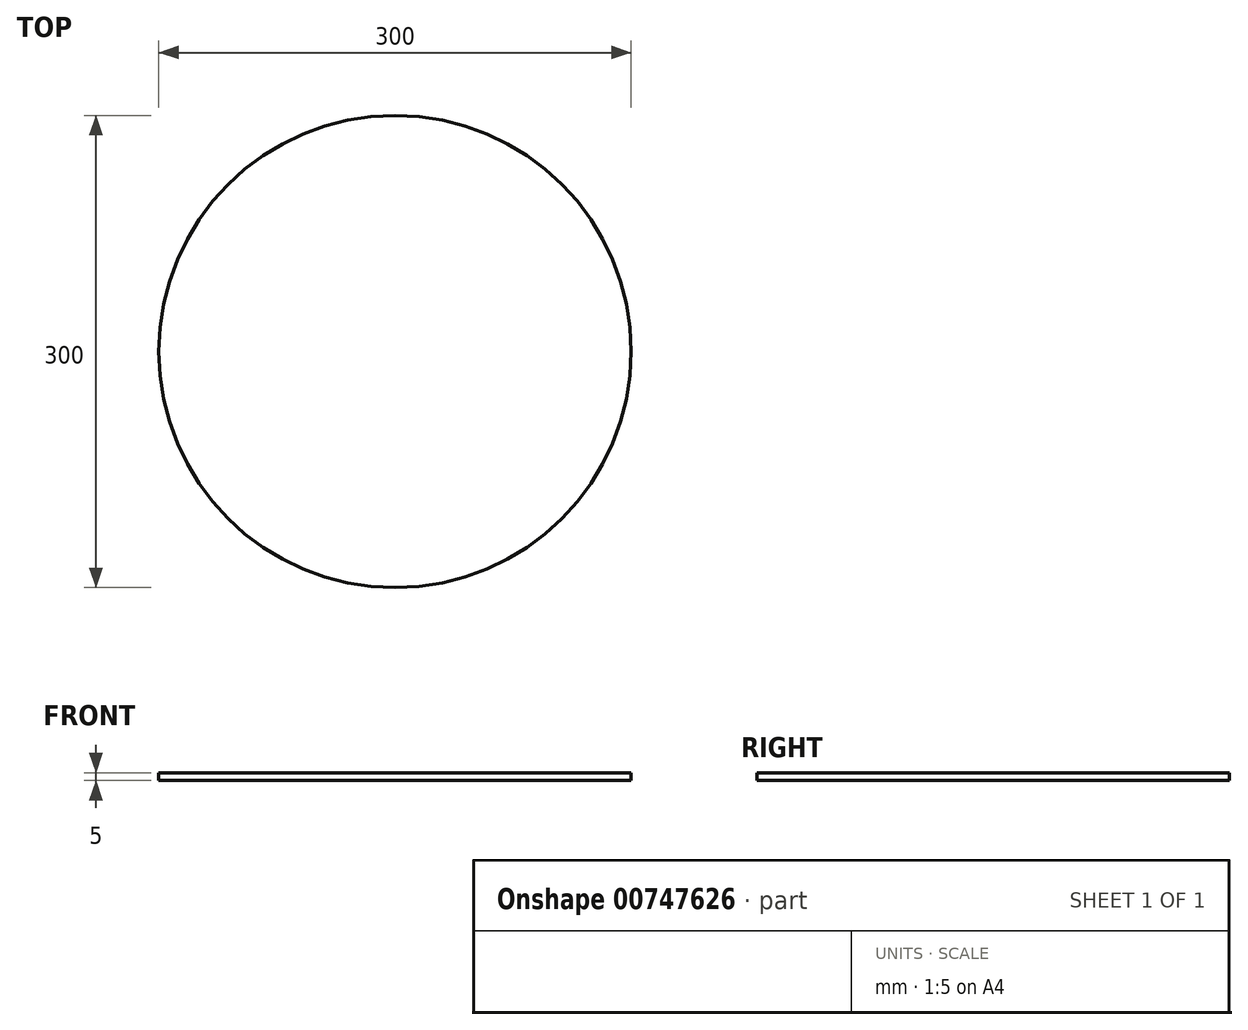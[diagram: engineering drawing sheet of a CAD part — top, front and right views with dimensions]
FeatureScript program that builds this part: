
annotation { "Feature Type Name" : "Feature", "Feature Type Description" : "" }
export const myFeature = defineFeature(function(context is Context, id is Id, definition is map)
    precondition{}
    {
        {
            var Q0;
            Q0=qCreatedBy(makeId("Top.planeOp"),FACE);
            var sketch = newSketch(context, id + "F0", { "sketchPlane" : qUnion([Q0])});
            skCircle(sketch, "E0", {"center": v(0, 0) * mm, "radius": 150 * mm});
            skSolve(sketch);
        }
        {
            var Q0;
            Q0 = qSketchRegion(id + "F0", true);
            extrude(context, id + "F1", {"entities" : qUnion([Q0]), "depth" : 5 * mm, "offsetDistance" : 25.4 * mm});
        }
    });
